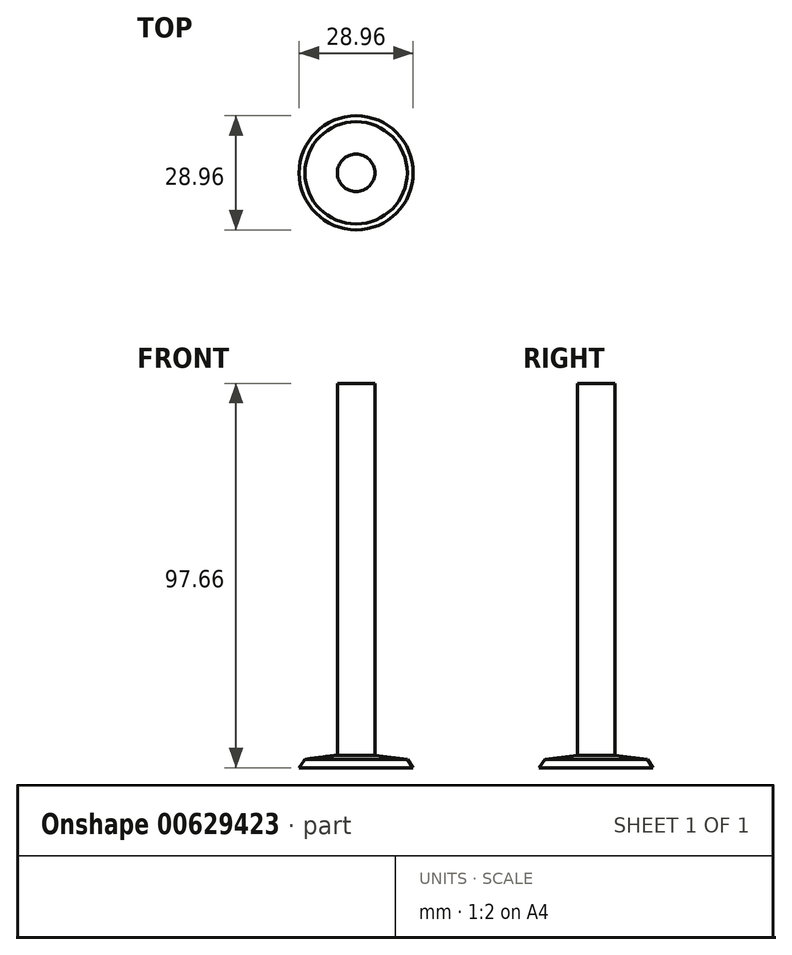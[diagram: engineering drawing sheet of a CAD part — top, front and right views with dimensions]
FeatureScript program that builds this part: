
annotation { "Feature Type Name" : "Feature", "Feature Type Description" : "" }
export const myFeature = defineFeature(function(context is Context, id is Id, definition is map)
    precondition{}
    {
        {
            var Q0;
            Q0=qCreatedBy(makeId("Top.planeOp"),FACE);
            var sketch = newSketch(context, id + "F0", { "sketchPlane" : qUnion([Q0])});
            skCircle(sketch, "E0", {"center": v(0, 0) * mm, "radius": 14.29 * mm});
            skSolve(sketch);
        }
        {
            var Q0;
            Q0=qCreatedBy(makeId("Front.planeOp"),FACE);
            var sketch = newSketch(context, id + "F1", { "sketchPlane" : qUnion([Q0])});
            skLineSegment(sketch, "E1", {"start": v(0, 0) * mm, "end": v(0, 61.95) * mm});
            skLineSegment(sketch, "E2.bottom", {"start": v(4.76, 59.56) * mm, "end": v(-4.76, 59.56) * mm});
            skLineSegment(sketch, "E2.top", {"start": v(4.76, -59.56) * mm, "end": v(-4.76, -59.56) * mm});
            skLineSegment(sketch, "E2.left", {"start": v(4.76, 59.56) * mm, "end": v(4.76, 3.19) * mm});
            skLineSegment(sketch, "E2.right", {"start": v(-4.76, 59.56) * mm, "end": v(-4.76, -59.56) * mm});
            skPoint(sketch, "E2.middle", {"position": v(0, 0) * mm});
            skLineSegment(sketch, "E3", {"start": v(0, 0) * mm, "end": v(14.48, 0) * mm});
            skLineSegment(sketch, "E4", {"start": v(14.48, 0) * mm, "end": v(13, 2.11) * mm});
            skLineSegment(sketch, "E5", {"start": v(13, 2.11) * mm, "end": v(4.76, 3.19) * mm});
            skLineSegment(sketch, "E6.trimOffspring", {"start": v(4.76, 0) * mm, "end": v(4.76, -59.56) * mm});
            skSolve(sketch);
        }
        {
            var Q0;
            {var subQ0=sQuery(id+"F1.wireOp",EDGE,"E2.left");Q0=makeQuery(id+"F1.imprint","IMPRINT",FACE,{"disambiguationData":[TD([[makeQuery(id+"F1.imprint","IMPRINT",EDGE,{"derivedFrom":subQ0}),-1.0]])]});}
            var Q1;
            Q1=sQuery(id+"F0.wireOp",EDGE,"E0");
            revolve(context, id + "F2", {"entities" : qUnion([Q0]), "axis" : qUnion([Q1]), "revolveType" : RevolveType.FULL});
        }
        {
            var Q0;
            Q0=makeQuery(id+"F2.opRevolve","SWEPT_FACE",FACE,{"disambiguationData":[OSD([sQuery(id+"F1.wireOp",EDGE,"E2.bottom")])]});
            extrude(context, id + "F3", {"entities" : qUnion([Q0]), "operationType" : NewBodyOperationType.ADD, "depth" : 38.1 * mm, "offsetDistance" : 25.4 * mm});
        }
    });
